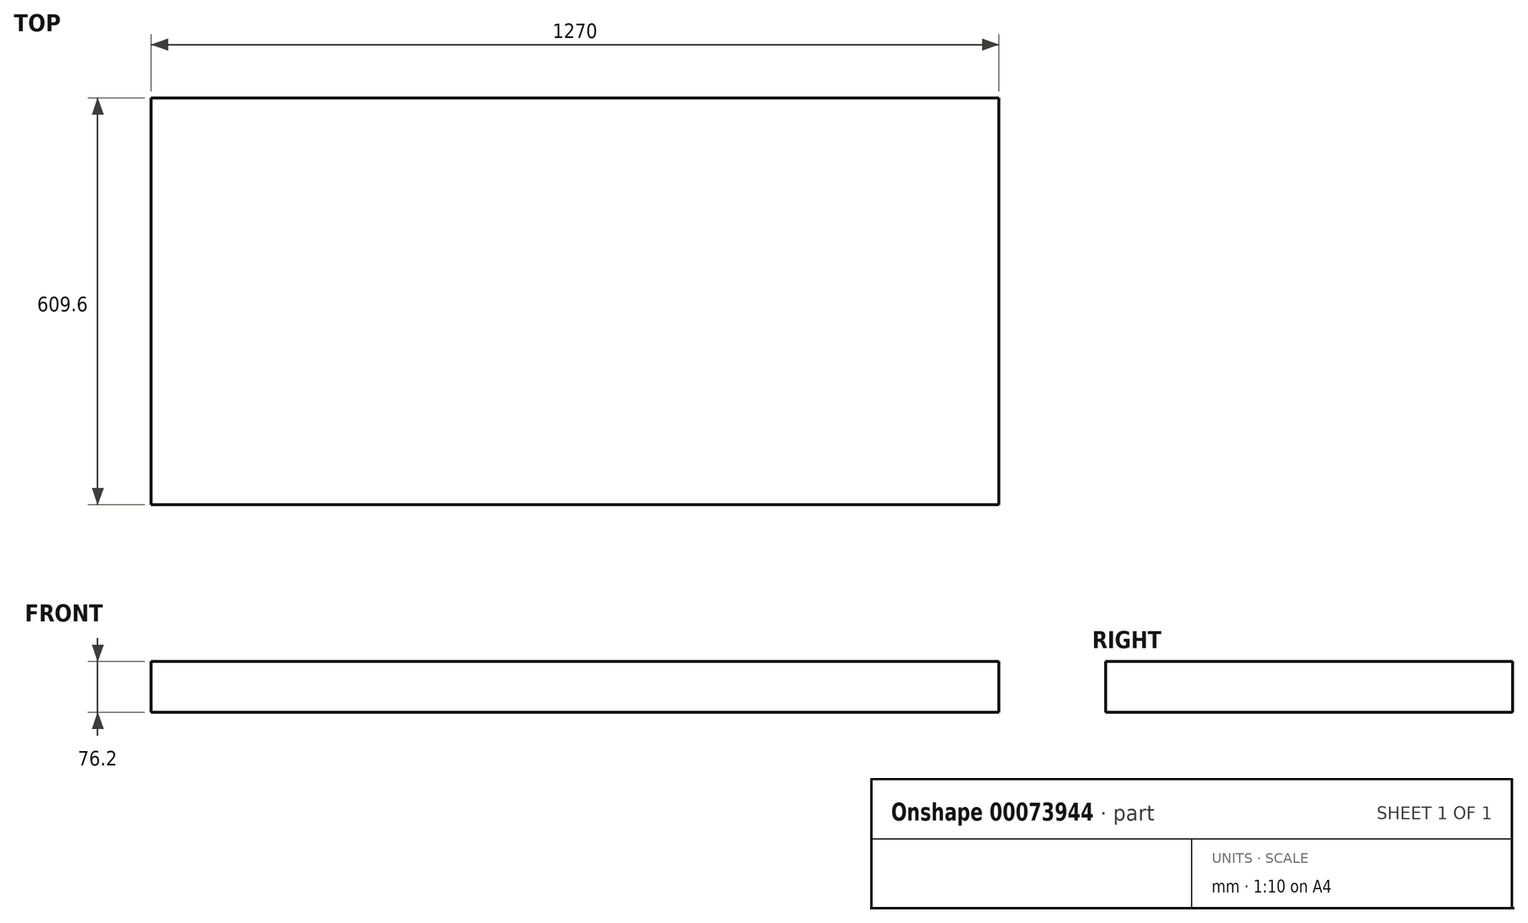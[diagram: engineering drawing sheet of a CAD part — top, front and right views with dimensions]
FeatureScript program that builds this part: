
annotation { "Feature Type Name" : "Feature", "Feature Type Description" : "" }
export const myFeature = defineFeature(function(context is Context, id is Id, definition is map)
    precondition{}
    {
        {
            var Q0;
            Q0=qCreatedBy(makeId("Top.planeOp"),FACE);
            var sketch = newSketch(context, id + "F0", { "sketchPlane" : qUnion([Q0])});
            skLineSegment(sketch, "E0.rect.bottom", {"start": v(-635, 304.8) * mm, "end": v(635, 304.8) * mm});
            skLineSegment(sketch, "E0.rect.top", {"start": v(-635, -304.8) * mm, "end": v(635, -304.8) * mm});
            skLineSegment(sketch, "E0.rect.left", {"start": v(-635, 304.8) * mm, "end": v(-635, -304.8) * mm});
            skLineSegment(sketch, "E0.rect.right", {"start": v(635, 304.8) * mm, "end": v(635, -304.8) * mm});
            skPoint(sketch, "E0.rect.middle", {"position": v(0, 0) * mm});
            skSolve(sketch);
        }
        {
            var Q0;
            Q0=makeQuery(id+"F0.imprint","IMPRINT",FACE,{"disambiguationData":[TD([[makeQuery(id+"F0.imprint","IMPRINT",EDGE,{"derivedFrom":sQuery(id+"F0.wireOp",EDGE,"E0.rect.bottom")}),-1.0]])]});
            extrude(context, id + "F1", {"entities" : qUnion([Q0]), "depth" : 76.2 * mm});
        }
    });
